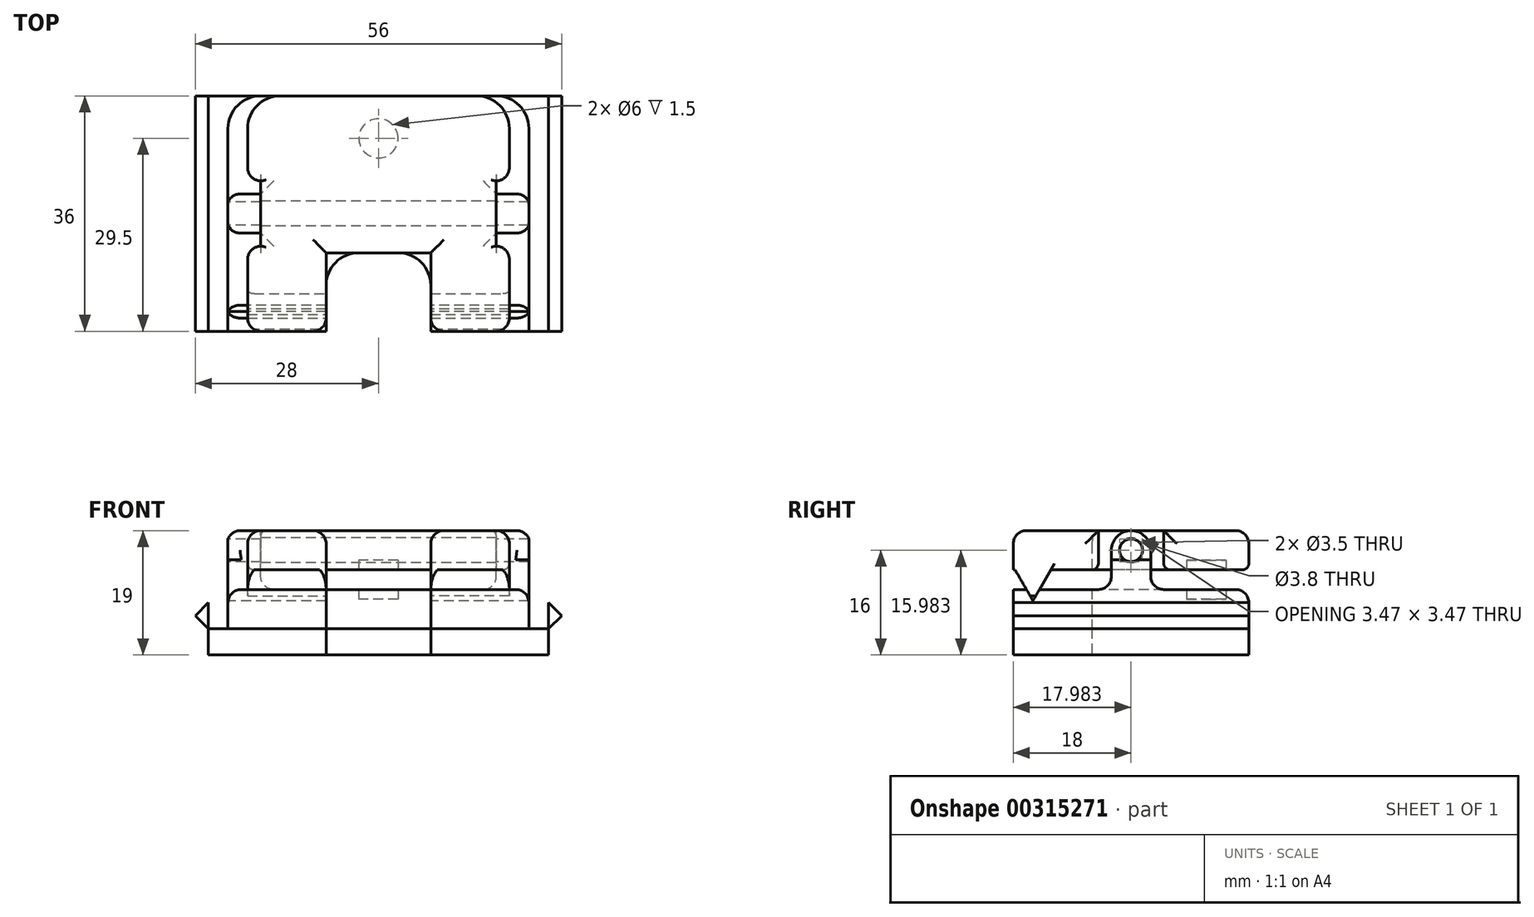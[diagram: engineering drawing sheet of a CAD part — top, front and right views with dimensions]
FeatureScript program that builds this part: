
annotation { "Feature Type Name" : "Feature", "Feature Type Description" : "" }
export const myFeature = defineFeature(function(context is Context, id is Id, definition is map)
    precondition{}
    {
        {
            var Q0;
            Q0=qCreatedBy(makeId("Top.planeOp"),FACE);
            var sketch = newSketch(context, id + "F0", { "sketchPlane" : qUnion([Q0])});
            skLineSegment(sketch, "E0.bottom", {"start": v(23, -18) * mm, "end": v(8, -18) * mm});
            skLineSegment(sketch, "E0.top", {"start": v(23, 18) * mm, "end": v(-23, 18) * mm});
            skLineSegment(sketch, "E0.left", {"start": v(23, -18) * mm, "end": v(23, 18) * mm});
            skLineSegment(sketch, "E0.right", {"start": v(-23, -18) * mm, "end": v(-23, 18) * mm});
            skPoint(sketch, "E0.middle", {"position": v(0, 0) * mm});
            skPoint(sketch, "E1.endSnap0", {"position": v(0, -18) * mm});
            skLineSegment(sketch, "E2", {"start": v(0, -6) * mm, "end": v(8, -6) * mm});
            skLineSegment(sketch, "E3", {"start": v(0, -6) * mm, "end": v(-8, -6) * mm});
            skLineSegment(sketch, "E4", {"start": v(-8, -6) * mm, "end": v(-8, -18) * mm});
            skLineSegment(sketch, "E5", {"start": v(8, -6) * mm, "end": v(8, -18) * mm});
            skLineSegment(sketch, "E6.trimOffspring", {"start": v(-8, -18) * mm, "end": v(-23, -18) * mm});
            skSolve(sketch);
        }
        {
            var Q0;
            Q0 = qSketchRegion(id + "F0", true);
            extrude(context, id + "F1", {"entities" : qUnion([Q0]), "depth" : 6 * mm});
        }
        {
            var Q0;
            Q0=qCreatedBy(makeId("Right.planeOp"),FACE);
            var sketch = newSketch(context, id + "F2", { "sketchPlane" : qUnion([Q0])});
            skCircle(sketch, "E7.cCircle", {"center": v(0, 0) * mm, "radius": 3.36 * mm, "construction": true});
            skLineSegment(sketch, "E7.0", {"start": v(5.82, -3.36) * mm, "end": v(-5.82, -3.36) * mm});
            skLineSegment(sketch, "E7.1", {"start": v(-5.82, -3.36) * mm, "end": v(0, 6.72) * mm});
            skLineSegment(sketch, "E7.2", {"start": v(0, 6.72) * mm, "end": v(5.82, -3.36) * mm});
            skPoint(sketch, "E7.0.midPoint", {"position": v(0, -3.36) * mm});
            skSolve(sketch);
        }
        {
            var Q0;
            Q0 = qSketchRegion(id + "F2", true);
            extrude(context, id + "F3", {"entities" : qUnion([Q0]), "endBound" : BoundingType.SYMMETRIC, "depth" : 80 * mm});
        }
        {
            var Q0;
            Q0=qCreatedBy(makeId("Top.planeOp"),FACE);
            var sketch = newSketch(context, id + "F4", { "sketchPlane" : qUnion([Q0])});
            skLineSegment(sketch, "E8", {"start": v(0, 0) * mm, "end": v(58.84, 0) * mm, "construction": true});
            skSolve(sketch);
        }
        {
            var Q0;
            Q0=makeQuery(id+"F3.opExtrude","SWEPT_BODY",BODY,{"disambiguationData":[OSD([sQuery(id+"F2.wireOp",EDGE,"E7.0"),sQuery(id+"F2.wireOp",EDGE,"E7.1"),sQuery(id+"F2.wireOp",EDGE,"E7.2")])]});
            transform(context, id + "F5", {"entities" : qUnion([Q0]), "transformType" : TransformType.COPY});
        }
        {
            var Q0;
            Q0=makeQuery(id+"F3.opExtrude","SWEPT_BODY",BODY,{"disambiguationData":[OSD([sQuery(id+"F2.wireOp",EDGE,"E7.0"),sQuery(id+"F2.wireOp",EDGE,"E7.1"),sQuery(id+"F2.wireOp",EDGE,"E7.2")])]});
            var Q1;
            Q1=sQuery(id+"F4.wireOp",EDGE,"E8");
            transform(context, id + "F6", {"entities" : qUnion([Q0]), "transformType" : TransformType.ROTATION, "transformAxis" : qUnion([Q1]), "angle" : 180 * degree, "makeCopy" : false});
        }
        {
            var Q0;
            Q0=makeQuery(id+"F3.opExtrude","SWEPT_BODY",BODY,{"disambiguationData":[OSD([sQuery(id+"F2.wireOp",EDGE,"E7.0"),sQuery(id+"F2.wireOp",EDGE,"E7.1"),sQuery(id+"F2.wireOp",EDGE,"E7.2")])]});
            transform(context, id + "F7", {"entities" : qUnion([Q0]), "transformType" : TransformType.TRANSLATION_3D, "dx" : 0 * mm, "dy" : -15 * mm, "dz" : 11 * mm, "makeCopy" : false});
        }
        {
            var Q0;
            Q0=qCreatedBy(makeId("Top.planeOp"),FACE);
            var sketch = newSketch(context, id + "F8", { "sketchPlane" : qUnion([Q0])});
            skLineSegment(sketch, "E9.bottom", {"start": v(45, -5) * mm, "end": v(-45, -5) * mm});
            skLineSegment(sketch, "E9.top", {"start": v(45, 5) * mm, "end": v(-45, 5) * mm});
            skLineSegment(sketch, "E9.left", {"start": v(45, -5) * mm, "end": v(45, 5) * mm});
            skLineSegment(sketch, "E9.right", {"start": v(-45, -5) * mm, "end": v(-45, 5) * mm});
            skPoint(sketch, "E9.middle", {"position": v(0, 0) * mm});
            skSolve(sketch);
        }
        {
            var Q0;
            Q0 = qSketchRegion(id + "F8", true);
            extrude(context, id + "F9", {"entities" : qUnion([Q0]), "depth" : 10 * mm});
        }
        {
            var Q0;
            Q0=makeQuery(id+"F9.opExtrude","SWEPT_BODY",BODY,{"disambiguationData":[OSD([sQuery(id+"F8.wireOp",EDGE,"E9.bottom"),sQuery(id+"F8.wireOp",EDGE,"E9.top"),sQuery(id+"F8.wireOp",EDGE,"E9.left"),sQuery(id+"F8.wireOp",EDGE,"E9.right")])]});
            transform(context, id + "F10", {"entities" : qUnion([Q0]), "transformType" : TransformType.TRANSLATION_3D, "dx" : 0 * mm, "dy" : 0 * mm, "dz" : 6 * mm, "makeCopy" : false});
        }
        {
            var Q0;
            Q0=makeQuery(id+"F9.opExtrude","SWEPT_BODY",BODY,{"disambiguationData":[OSD([sQuery(id+"F8.wireOp",EDGE,"E9.bottom"),sQuery(id+"F8.wireOp",EDGE,"E9.top"),sQuery(id+"F8.wireOp",EDGE,"E9.left"),sQuery(id+"F8.wireOp",EDGE,"E9.right")])]});
            var Q1;
            Q1=makeQuery(id+"F5.opPattern","COPY",BODY,{"derivedFrom":makeQuery(id+"F3.opExtrude","SWEPT_BODY",BODY,{"disambiguationData":[OSD([sQuery(id+"F2.wireOp",EDGE,"E7.0"),sQuery(id+"F2.wireOp",EDGE,"E7.1"),sQuery(id+"F2.wireOp",EDGE,"E7.2")])]}),"instanceName":"1"});
            booleanBodies(context, id + "F11", {"operationType" : BooleanOperationType.SUBTRACTION, "tools" : qUnion([Q0]), "targets" : qUnion([Q1])});
        }
        {
            var Q0;
            Q0=makeQuery(id+"F3.opExtrude","SWEPT_BODY",BODY,{"disambiguationData":[OSD([sQuery(id+"F2.wireOp",EDGE,"E7.0"),sQuery(id+"F2.wireOp",EDGE,"E7.1"),sQuery(id+"F2.wireOp",EDGE,"E7.2")])]});
            var Q1;
            Q1=makeQuery(id+"F1.opExtrude","SWEPT_BODY",BODY,{"disambiguationData":[OSD([sQuery(id+"F0.wireOp",EDGE,"E0.bottom"),sQuery(id+"F0.wireOp",EDGE,"E0.top"),sQuery(id+"F0.wireOp",EDGE,"E0.left"),sQuery(id+"F0.wireOp",EDGE,"E0.right"),sQuery(id+"F0.wireOp",EDGE,"E2"),sQuery(id+"F0.wireOp",EDGE,"E3"),sQuery(id+"F0.wireOp",EDGE,"E4"),sQuery(id+"F0.wireOp",EDGE,"E5"),sQuery(id+"F0.wireOp",EDGE,"E6.trimOffspring")])]});
            booleanBodies(context, id + "F12", {"operationType" : BooleanOperationType.SUBTRACTION, "tools" : qUnion([Q0]), "targets" : qUnion([Q1])});
        }
        {
            var Q0;
            Q0=qCreatedBy(makeId("Top.planeOp"),FACE);
            var sketch = newSketch(context, id + "F13", { "sketchPlane" : qUnion([Q0])});
            skLineSegment(sketch, "E10", {"start": v(0, 0) * mm, "end": v(55.34, 0) * mm, "construction": true});
            skSolve(sketch);
        }
        {
            var Q0;
            Q0=makeQuery(id+"F5.opPattern","COPY",BODY,{"derivedFrom":makeQuery(id+"F3.opExtrude","SWEPT_BODY",BODY,{"disambiguationData":[OSD([sQuery(id+"F2.wireOp",EDGE,"E7.0"),sQuery(id+"F2.wireOp",EDGE,"E7.1"),sQuery(id+"F2.wireOp",EDGE,"E7.2")])]}),"instanceName":"1"});
            var Q1;
            Q1=sQuery(id+"F13.wireOp",EDGE,"E10");
            transform(context, id + "F14", {"entities" : qUnion([Q0]), "transformType" : TransformType.ROTATION, "transformAxis" : qUnion([Q1]), "angle" : 180 * degree, "makeCopy" : false});
        }
        {
            var Q0;
            Q0=makeQuery(id+"F5.opPattern","COPY",BODY,{"derivedFrom":makeQuery(id+"F3.opExtrude","SWEPT_BODY",BODY,{"disambiguationData":[OSD([sQuery(id+"F2.wireOp",EDGE,"E7.0"),sQuery(id+"F2.wireOp",EDGE,"E7.1"),sQuery(id+"F2.wireOp",EDGE,"E7.2")])]}),"instanceName":"1"});
            transform(context, id + "F15", {"entities" : qUnion([Q0]), "transformType" : TransformType.TRANSLATION_3D, "dx" : 0 * mm, "dy" : -15 * mm, "dz" : 11 * mm, "makeCopy" : false});
        }
        {
            var Q0;
            Q0=qCreatedBy(makeId("Top.planeOp"),FACE);
            var sketch = newSketch(context, id + "F16", { "sketchPlane" : qUnion([Q0])});
            skLineSegment(sketch, "E11.bottom", {"start": v(20, -18) * mm, "end": v(-20, -18) * mm});
            skLineSegment(sketch, "E11.top", {"start": v(20, 18) * mm, "end": v(-20, 18) * mm});
            skLineSegment(sketch, "E11.left", {"start": v(20, -18) * mm, "end": v(20, 18) * mm});
            skLineSegment(sketch, "E11.right", {"start": v(-20, -18) * mm, "end": v(-20, 18) * mm});
            skPoint(sketch, "E11.middle", {"position": v(0, 0) * mm});
            skSolve(sketch);
        }
        {
            var Q0;
            Q0 = qSketchRegion(id + "F16", true);
            extrude(context, id + "F17", {"entities" : qUnion([Q0]), "depth" : 6 * mm});
        }
        {
            var Q0;
            Q0=qCreatedBy(makeId("Top.planeOp"),FACE);
            var sketch = newSketch(context, id + "F18", { "sketchPlane" : qUnion([Q0])});
            skLineSegment(sketch, "E12", {"start": v(0, 0) * mm, "end": v(0, -6) * mm});
            skLineSegment(sketch, "E13", {"start": v(0, -6) * mm, "end": v(8, -6) * mm});
            skLineSegment(sketch, "E14", {"start": v(8, -6) * mm, "end": v(8, -18) * mm});
            skLineSegment(sketch, "E15", {"start": v(8, -18) * mm, "end": v(-8, -18) * mm});
            skLineSegment(sketch, "E16", {"start": v(-8, -18) * mm, "end": v(-8, -6) * mm});
            skLineSegment(sketch, "E17", {"start": v(-8, -6) * mm, "end": v(0, -6) * mm});
            skSolve(sketch);
        }
        {
            var Q0;
            Q0 = qSketchRegion(id + "F18", true);
            extrude(context, id + "F19", {"entities" : qUnion([Q0]), "depth" : 25 * mm});
        }
        {
            var Q0;
            Q0=makeQuery(id+"F19.opExtrude","SWEPT_BODY",BODY,{"disambiguationData":[OSD([sQuery(id+"F18.wireOp",EDGE,"E13"),sQuery(id+"F18.wireOp",EDGE,"E14"),sQuery(id+"F18.wireOp",EDGE,"E15"),sQuery(id+"F18.wireOp",EDGE,"E16"),sQuery(id+"F18.wireOp",EDGE,"E17")])]});
            var Q1;
            Q1=makeQuery(id+"F17.opExtrude","SWEPT_BODY",BODY,{"disambiguationData":[OSD([sQuery(id+"F16.wireOp",EDGE,"E11.bottom"),sQuery(id+"F16.wireOp",EDGE,"E11.top"),sQuery(id+"F16.wireOp",EDGE,"E11.left"),sQuery(id+"F16.wireOp",EDGE,"E11.right")])]});
            booleanBodies(context, id + "F20", {"operationType" : BooleanOperationType.SUBTRACTION, "tools" : qUnion([Q0]), "targets" : qUnion([Q1])});
        }
        {
            var Q0;
            Q0=makeQuery(id+"F17.opExtrude","SWEPT_BODY",BODY,{"disambiguationData":[OSD([sQuery(id+"F16.wireOp",EDGE,"E11.bottom"),sQuery(id+"F16.wireOp",EDGE,"E11.top"),sQuery(id+"F16.wireOp",EDGE,"E11.left"),sQuery(id+"F16.wireOp",EDGE,"E11.right")])]});
            transform(context, id + "F21", {"entities" : qUnion([Q0]), "transformType" : TransformType.TRANSLATION_3D, "dx" : 0 * mm, "dy" : 0 * mm, "dz" : 9 * mm, "makeCopy" : false});
        }
        {
            var Q0;
            Q0=qCreatedBy(makeId("Top.planeOp"),FACE);
            var sketch = newSketch(context, id + "F22", { "sketchPlane" : qUnion([Q0])});
            skLineSegment(sketch, "E18", {"start": v(0, 0) * mm, "end": v(0, -9) * mm});
            skLineSegment(sketch, "E19", {"start": v(0, -9) * mm, "end": v(8, -9) * mm});
            skLineSegment(sketch, "E20", {"start": v(8, -9) * mm, "end": v(8, -21) * mm});
            skLineSegment(sketch, "E21", {"start": v(8, -21) * mm, "end": v(-8, -21) * mm});
            skLineSegment(sketch, "E22", {"start": v(-8, -21) * mm, "end": v(-8, -9) * mm});
            skLineSegment(sketch, "E23", {"start": v(-8, -9) * mm, "end": v(0, -9) * mm});
            skLineSegment(sketch, "E24", {"start": v(8, -9) * mm, "end": v(20, -9) * mm});
            skLineSegment(sketch, "E25", {"start": v(20, -9) * mm, "end": v(20, -21) * mm});
            skLineSegment(sketch, "E26", {"start": v(20, -21) * mm, "end": v(42, -21) * mm});
            skLineSegment(sketch, "E27", {"start": v(42, -21) * mm, "end": v(42, -9) * mm});
            skLineSegment(sketch, "E28", {"start": v(42, -9) * mm, "end": v(20, -9) * mm});
            skLineSegment(sketch, "E29", {"start": v(-8, -9) * mm, "end": v(-20, -9) * mm});
            skLineSegment(sketch, "E30", {"start": v(-20, -9) * mm, "end": v(-20, -21) * mm});
            skLineSegment(sketch, "E31", {"start": v(-20, -21) * mm, "end": v(-42, -21) * mm});
            skLineSegment(sketch, "E32", {"start": v(-42, -21) * mm, "end": v(-42, -9) * mm});
            skLineSegment(sketch, "E33", {"start": v(-42, -9) * mm, "end": v(-20, -9) * mm});
            skSolve(sketch);
        }
        {
            var Q0;
            Q0 = qSketchRegion(id + "F22", true);
            extrude(context, id + "F23", {"entities" : qUnion([Q0]), "depth" : 25 * mm});
        }
        {
            var Q0;
            Q0=makeQuery(id+"F23.opExtrude","SWEPT_BODY",BODY,{"disambiguationData":[OSD([sQuery(id+"F22.wireOp",EDGE,"E30"),sQuery(id+"F22.wireOp",EDGE,"E31"),sQuery(id+"F22.wireOp",EDGE,"E32"),sQuery(id+"F22.wireOp",EDGE,"E33")])]});
            var Q1;
            Q1=makeQuery(id+"F23.opExtrude","SWEPT_BODY",BODY,{"disambiguationData":[OSD([sQuery(id+"F22.wireOp",EDGE,"E19"),sQuery(id+"F22.wireOp",EDGE,"E20"),sQuery(id+"F22.wireOp",EDGE,"E21"),sQuery(id+"F22.wireOp",EDGE,"E22"),sQuery(id+"F22.wireOp",EDGE,"E23")])]});
            var Q2;
            Q2=makeQuery(id+"F23.opExtrude","SWEPT_BODY",BODY,{"disambiguationData":[OSD([sQuery(id+"F22.wireOp",EDGE,"E25"),sQuery(id+"F22.wireOp",EDGE,"E26"),sQuery(id+"F22.wireOp",EDGE,"E27"),sQuery(id+"F22.wireOp",EDGE,"E28")])]});
            var Q3;
            Q3=makeQuery(id+"F5.opPattern","COPY",BODY,{"derivedFrom":makeQuery(id+"F3.opExtrude","SWEPT_BODY",BODY,{"disambiguationData":[OSD([sQuery(id+"F2.wireOp",EDGE,"E7.0"),sQuery(id+"F2.wireOp",EDGE,"E7.1"),sQuery(id+"F2.wireOp",EDGE,"E7.2")])]}),"instanceName":"1"});
            booleanBodies(context, id + "F24", {"operationType" : BooleanOperationType.SUBTRACTION, "tools" : qUnion([Q0, Q1, Q2]), "targets" : qUnion([Q3])});
        }
        {
            var Q0;
            Q0=qCreatedBy(makeId("Top.planeOp"),FACE);
            var sketch = newSketch(context, id + "F25", { "sketchPlane" : qUnion([Q0])});
            skLineSegment(sketch, "E34", {"start": v(0, 0) * mm, "end": v(20, 0) * mm});
            skLineSegment(sketch, "E35", {"start": v(20, 0) * mm, "end": v(20, -18) * mm});
            skLineSegment(sketch, "E36", {"start": v(20, -18) * mm, "end": v(20, -23) * mm});
            skLineSegment(sketch, "E37", {"start": v(20, -23) * mm, "end": v(-20, -23) * mm});
            skLineSegment(sketch, "E38", {"start": v(-20, -23) * mm, "end": v(-20, -18) * mm});
            skLineSegment(sketch, "E39", {"start": v(-20, -18) * mm, "end": v(20, -18) * mm});
            skSolve(sketch);
        }
        {
            var Q0;
            Q0 = qSketchRegion(id + "F25", true);
            extrude(context, id + "F26", {"entities" : qUnion([Q0]), "depth" : 25 * mm});
        }
        {
            var Q0;
            Q0=makeQuery(id+"F26.opExtrude","SWEPT_BODY",BODY,{"disambiguationData":[OSD([sQuery(id+"F25.wireOp",EDGE,"E36"),sQuery(id+"F25.wireOp",EDGE,"E37"),sQuery(id+"F25.wireOp",EDGE,"E38"),sQuery(id+"F25.wireOp",EDGE,"E39")])]});
            var Q1;
            Q1=makeQuery(id+"F24.opBoolean","SPLIT",BODY,{"disambiguationData":[OD(1.0)],"derivedFrom":makeQuery(id+"F5.opPattern","COPY",BODY,{"derivedFrom":makeQuery(id+"F3.opExtrude","SWEPT_BODY",BODY,{"disambiguationData":[OSD([sQuery(id+"F2.wireOp",EDGE,"E7.0"),sQuery(id+"F2.wireOp",EDGE,"E7.1"),sQuery(id+"F2.wireOp",EDGE,"E7.2")])]}),"instanceName":"1"})});
            var Q2;
            Q2=makeQuery(id+"F24.opBoolean","SPLIT",BODY,{"disambiguationData":[OD(0.0)],"derivedFrom":makeQuery(id+"F5.opPattern","COPY",BODY,{"derivedFrom":makeQuery(id+"F3.opExtrude","SWEPT_BODY",BODY,{"disambiguationData":[OSD([sQuery(id+"F2.wireOp",EDGE,"E7.0"),sQuery(id+"F2.wireOp",EDGE,"E7.1"),sQuery(id+"F2.wireOp",EDGE,"E7.2")])]}),"instanceName":"1"})});
            booleanBodies(context, id + "F27", {"operationType" : BooleanOperationType.SUBTRACTION, "tools" : qUnion([Q0]), "targets" : qUnion([Q1, Q2])});
        }
        {
            var Q0;
            Q0=makeQuery(id+"F24.opBoolean","SPLIT",BODY,{"disambiguationData":[OD(0.0)],"derivedFrom":makeQuery(id+"F5.opPattern","COPY",BODY,{"derivedFrom":makeQuery(id+"F3.opExtrude","SWEPT_BODY",BODY,{"disambiguationData":[OSD([sQuery(id+"F2.wireOp",EDGE,"E7.0"),sQuery(id+"F2.wireOp",EDGE,"E7.1"),sQuery(id+"F2.wireOp",EDGE,"E7.2")])]}),"instanceName":"1"})});
            var Q1;
            Q1=makeQuery(id+"F24.opBoolean","SPLIT",BODY,{"disambiguationData":[OD(1.0)],"derivedFrom":makeQuery(id+"F5.opPattern","COPY",BODY,{"derivedFrom":makeQuery(id+"F3.opExtrude","SWEPT_BODY",BODY,{"disambiguationData":[OSD([sQuery(id+"F2.wireOp",EDGE,"E7.0"),sQuery(id+"F2.wireOp",EDGE,"E7.1"),sQuery(id+"F2.wireOp",EDGE,"E7.2")])]}),"instanceName":"1"})});
            var Q2;
            Q2=makeQuery(id+"F17.opExtrude","SWEPT_BODY",BODY,{"disambiguationData":[OSD([sQuery(id+"F16.wireOp",EDGE,"E11.bottom"),sQuery(id+"F16.wireOp",EDGE,"E11.top"),sQuery(id+"F16.wireOp",EDGE,"E11.left"),sQuery(id+"F16.wireOp",EDGE,"E11.right")])]});
            booleanBodies(context, id + "F28", {"operationType" : BooleanOperationType.UNION, "tools" : qUnion([Q0, Q1, Q2])});
        }
        {
            var Q0;
            Q0=qCreatedBy(makeId("Right.planeOp"),FACE);
            var sketch = newSketch(context, id + "F29", { "sketchPlane" : qUnion([Q0])});
            skArc(sketch, "E40", {"start": v(3, 12) * mm, "mid": v(0, 15) * mm, "end": v(-3, 12) * mm});
            skLineSegment(sketch, "E41", {"start": v(0, 0) * mm, "end": v(3, 0) * mm});
            skLineSegment(sketch, "E42", {"start": v(3, 0) * mm, "end": v(3, 12) * mm});
            skLineSegment(sketch, "E43", {"start": v(0, 0) * mm, "end": v(-3, 0) * mm});
            skLineSegment(sketch, "E44", {"start": v(-3, 0) * mm, "end": v(-3, 12) * mm});
            skCircle(sketch, "E45", {"center": v(0, 12) * mm, "radius": 1.75 * mm});
            skSolve(sketch);
        }
        {
            var Q0;
            Q0 = qSketchRegion(id + "F29", true);
            extrude(context, id + "F30", {"entities" : qUnion([Q0]), "endBound" : BoundingType.SYMMETRIC, "depth" : 5 * mm});
        }
        {
            var Q0;
            Q0=makeQuery(id+"F30.opExtrude","SWEPT_BODY",BODY,{"disambiguationData":[OSD([sQuery(id+"F29.wireOp",EDGE,"E40"),sQuery(id+"F29.wireOp",EDGE,"E41"),sQuery(id+"F29.wireOp",EDGE,"E42"),sQuery(id+"F29.wireOp",EDGE,"E43"),sQuery(id+"F29.wireOp",EDGE,"E44"),sQuery(id+"F29.wireOp",EDGE,"E45")])]});
            transform(context, id + "F31", {"entities" : qUnion([Q0]), "transformType" : TransformType.COPY});
        }
        {
            var Q0;
            Q0=makeQuery(id+"F31.opPattern","COPY",BODY,{"derivedFrom":makeQuery(id+"F30.opExtrude","SWEPT_BODY",BODY,{"disambiguationData":[OSD([sQuery(id+"F29.wireOp",EDGE,"E40"),sQuery(id+"F29.wireOp",EDGE,"E41"),sQuery(id+"F29.wireOp",EDGE,"E42"),sQuery(id+"F29.wireOp",EDGE,"E43"),sQuery(id+"F29.wireOp",EDGE,"E44"),sQuery(id+"F29.wireOp",EDGE,"E45")])]}),"instanceName":"1"});
            transform(context, id + "F32", {"entities" : qUnion([Q0]), "transformType" : TransformType.TRANSLATION_3D, "dx" : 20.5 * mm, "dy" : 0 * mm, "dz" : 0 * mm, "makeCopy" : false});
        }
        {
            var Q0;
            Q0=makeQuery(id+"F30.opExtrude","SWEPT_BODY",BODY,{"disambiguationData":[OSD([sQuery(id+"F29.wireOp",EDGE,"E40"),sQuery(id+"F29.wireOp",EDGE,"E41"),sQuery(id+"F29.wireOp",EDGE,"E42"),sQuery(id+"F29.wireOp",EDGE,"E43"),sQuery(id+"F29.wireOp",EDGE,"E44"),sQuery(id+"F29.wireOp",EDGE,"E45")])]});
            transform(context, id + "F33", {"entities" : qUnion([Q0]), "transformType" : TransformType.TRANSLATION_3D, "dx" : -20.5 * mm, "dy" : 0 * mm, "dz" : 0 * mm, "makeCopy" : false});
        }
        {
            var Q0;
            Q0=qCreatedBy(makeId("Top.planeOp"),FACE);
            var sketch = newSketch(context, id + "F34", { "sketchPlane" : qUnion([Q0])});
            skLineSegment(sketch, "E46.bottom", {"start": v(3, -5) * mm, "end": v(-3, -5) * mm});
            skLineSegment(sketch, "E46.top", {"start": v(3, 5) * mm, "end": v(-3, 5) * mm});
            skLineSegment(sketch, "E46.left", {"start": v(3, -5) * mm, "end": v(3, 5) * mm});
            skLineSegment(sketch, "E46.right", {"start": v(-3, -5) * mm, "end": v(-3, 5) * mm});
            skPoint(sketch, "E46.middle", {"position": v(0, 0) * mm});
            skSolve(sketch);
        }
        {
            var Q0;
            Q0 = qSketchRegion(id + "F34", true);
            extrude(context, id + "F35", {"entities" : qUnion([Q0]), "depth" : 25 * mm});
        }
        {
            var Q0;
            Q0=makeQuery(id+"F35.opExtrude","SWEPT_BODY",BODY,{"disambiguationData":[OSD([sQuery(id+"F34.wireOp",EDGE,"E46.bottom"),sQuery(id+"F34.wireOp",EDGE,"E46.top"),sQuery(id+"F34.wireOp",EDGE,"E46.left"),sQuery(id+"F34.wireOp",EDGE,"E46.right")])]});
            transform(context, id + "F36", {"entities" : qUnion([Q0]), "transformType" : TransformType.COPY});
        }
        {
            var Q0;
            Q0=makeQuery(id+"F36.opPattern","COPY",BODY,{"derivedFrom":makeQuery(id+"F35.opExtrude","SWEPT_BODY",BODY,{"disambiguationData":[OSD([sQuery(id+"F34.wireOp",EDGE,"E46.bottom"),sQuery(id+"F34.wireOp",EDGE,"E46.top"),sQuery(id+"F34.wireOp",EDGE,"E46.left"),sQuery(id+"F34.wireOp",EDGE,"E46.right")])]}),"instanceName":"1"});
            transform(context, id + "F37", {"entities" : qUnion([Q0]), "transformType" : TransformType.TRANSLATION_3D, "dx" : 21 * mm, "dy" : 0 * mm, "dz" : 0 * mm, "makeCopy" : false});
        }
        {
            var Q0;
            Q0=makeQuery(id+"F35.opExtrude","SWEPT_BODY",BODY,{"disambiguationData":[OSD([sQuery(id+"F34.wireOp",EDGE,"E46.bottom"),sQuery(id+"F34.wireOp",EDGE,"E46.top"),sQuery(id+"F34.wireOp",EDGE,"E46.left"),sQuery(id+"F34.wireOp",EDGE,"E46.right")])]});
            transform(context, id + "F38", {"entities" : qUnion([Q0]), "transformType" : TransformType.TRANSLATION_3D, "dx" : -21 * mm, "dy" : 0 * mm, "dz" : 0 * mm, "makeCopy" : false});
        }
        {
            var Q0;
            Q0=makeQuery(id+"F35.opExtrude","SWEPT_BODY",BODY,{"disambiguationData":[OSD([sQuery(id+"F34.wireOp",EDGE,"E46.bottom"),sQuery(id+"F34.wireOp",EDGE,"E46.top"),sQuery(id+"F34.wireOp",EDGE,"E46.left"),sQuery(id+"F34.wireOp",EDGE,"E46.right")])]});
            var Q1;
            Q1=makeQuery(id+"F36.opPattern","COPY",BODY,{"derivedFrom":makeQuery(id+"F35.opExtrude","SWEPT_BODY",BODY,{"disambiguationData":[OSD([sQuery(id+"F34.wireOp",EDGE,"E46.bottom"),sQuery(id+"F34.wireOp",EDGE,"E46.top"),sQuery(id+"F34.wireOp",EDGE,"E46.left"),sQuery(id+"F34.wireOp",EDGE,"E46.right")])]}),"instanceName":"1"});
            var Q2;
            Q2=makeQuery(id+"F24.opBoolean","SPLIT",BODY,{"disambiguationData":[OD(0.0)],"derivedFrom":makeQuery(id+"F5.opPattern","COPY",BODY,{"derivedFrom":makeQuery(id+"F3.opExtrude","SWEPT_BODY",BODY,{"disambiguationData":[OSD([sQuery(id+"F2.wireOp",EDGE,"E7.0"),sQuery(id+"F2.wireOp",EDGE,"E7.1"),sQuery(id+"F2.wireOp",EDGE,"E7.2")])]}),"instanceName":"1"})});
            booleanBodies(context, id + "F39", {"operationType" : BooleanOperationType.SUBTRACTION, "tools" : qUnion([Q0, Q1]), "targets" : qUnion([Q2])});
        }
        {
            var Q0;
            Q0=qCreatedBy(makeId("Right.planeOp"),FACE);
            var sketch = newSketch(context, id + "F40", { "sketchPlane" : qUnion([Q0])});
            skLineSegment(sketch, "E47", {"start": v(0, 0) * mm, "end": v(0, 12) * mm});
            skCircle(sketch, "E48", {"center": v(0, 12) * mm, "radius": 1.9 * mm});
            skSolve(sketch);
        }
        {
            var Q0;
            Q0 = qSketchRegion(id + "F40", true);
            extrude(context, id + "F41", {"entities" : qUnion([Q0]), "endBound" : BoundingType.SYMMETRIC, "depth" : 80 * mm});
        }
        {
            var Q0;
            Q0=makeQuery(id+"F41.opExtrude","SWEPT_BODY",BODY,{"disambiguationData":[OSD([sQuery(id+"F40.wireOp",EDGE,"E48")])]});
            var Q1;
            Q1=makeQuery(id+"F24.opBoolean","SPLIT",BODY,{"disambiguationData":[OD(0.0)],"derivedFrom":makeQuery(id+"F5.opPattern","COPY",BODY,{"derivedFrom":makeQuery(id+"F3.opExtrude","SWEPT_BODY",BODY,{"disambiguationData":[OSD([sQuery(id+"F2.wireOp",EDGE,"E7.0"),sQuery(id+"F2.wireOp",EDGE,"E7.1"),sQuery(id+"F2.wireOp",EDGE,"E7.2")])]}),"instanceName":"1"})});
            booleanBodies(context, id + "F42", {"operationType" : BooleanOperationType.SUBTRACTION, "tools" : qUnion([Q0]), "targets" : qUnion([Q1])});
        }
        {
            var Q0;
            Q0=qCreatedBy(makeId("Top.planeOp"),FACE);
            var sketch = newSketch(context, id + "F43", { "sketchPlane" : qUnion([Q0])});
            skCircle(sketch, "E49", {"center": v(0, 12.5) * mm, "radius": 3 * mm});
            skSolve(sketch);
        }
        {
            var Q0;
            Q0 = qSketchRegion(id + "F43", true);
            extrude(context, id + "F44", {"entities" : qUnion([Q0]), "depth" : 6 * mm});
        }
        {
            var Q0;
            Q0=makeQuery(id+"F44.opExtrude","SWEPT_BODY",BODY,{"disambiguationData":[OSD([sQuery(id+"F43.wireOp",EDGE,"E49")])]});
            transform(context, id + "F45", {"entities" : qUnion([Q0]), "transformType" : TransformType.TRANSLATION_3D, "dx" : 0 * mm, "dy" : -1 * mm, "dz" : 4.5 * mm, "makeCopy" : false});
        }
        {
            var Q0;
            Q0=makeQuery(id+"F44.opExtrude","SWEPT_BODY",BODY,{"disambiguationData":[OSD([sQuery(id+"F43.wireOp",EDGE,"E49")])]});
            var Q1;
            Q1=makeQuery(id+"F1.opExtrude","SWEPT_BODY",BODY,{"disambiguationData":[OSD([sQuery(id+"F0.wireOp",EDGE,"E0.bottom"),sQuery(id+"F0.wireOp",EDGE,"E0.top"),sQuery(id+"F0.wireOp",EDGE,"E0.left"),sQuery(id+"F0.wireOp",EDGE,"E0.right"),sQuery(id+"F0.wireOp",EDGE,"E2"),sQuery(id+"F0.wireOp",EDGE,"E3"),sQuery(id+"F0.wireOp",EDGE,"E4"),sQuery(id+"F0.wireOp",EDGE,"E5"),sQuery(id+"F0.wireOp",EDGE,"E6.trimOffspring")])]});
            var Q2;
            Q2=makeQuery(id+"F24.opBoolean","SPLIT",BODY,{"disambiguationData":[OD(0.0)],"derivedFrom":makeQuery(id+"F5.opPattern","COPY",BODY,{"derivedFrom":makeQuery(id+"F3.opExtrude","SWEPT_BODY",BODY,{"disambiguationData":[OSD([sQuery(id+"F2.wireOp",EDGE,"E7.0"),sQuery(id+"F2.wireOp",EDGE,"E7.1"),sQuery(id+"F2.wireOp",EDGE,"E7.2")])]}),"instanceName":"1"})});
            booleanBodies(context, id + "F46", {"operationType" : BooleanOperationType.SUBTRACTION, "tools" : qUnion([Q0]), "targets" : qUnion([Q1, Q2])});
        }
        {
            var Q0;
            Q0=qCreatedBy(makeId("Front.planeOp"),FACE);
            var sketch = newSketch(context, id + "F47", { "sketchPlane" : qUnion([Q0])});
            skLineSegment(sketch, "E50", {"start": v(0, 0) * mm, "end": v(10, 0) * mm});
            skLineSegment(sketch, "E51", {"start": v(10, 0) * mm, "end": v(10, 1.5) * mm});
            skText(sketch, "E52", { "text": "SF", "fontName": "OpenSans-Bold.ttf"});
            const initialGuessF47  = {"E52": [0.01, 0.0015, 1, 0, 0.0035]};
            skSetInitialGuess(sketch, initialGuessF47);
            skSolve(sketch);
        }
        {
            var Q0;
            Q0 = qSketchRegion(id + "F47", true);
            extrude(context, id + "F48", {"entities" : qUnion([Q0]), "depth" : 3 * mm});
        }
        {
            var Q0;
            Q0=makeQuery(id+"F48.opExtrude","SWEPT_BODY",BODY,{"disambiguationData":[OSD([sQuery(id+"F47.wireOp",EDGE,"E52.sketch_text.stroke-28"),sQuery(id+"F47.wireOp",EDGE,"E52.sketch_text.stroke-29"),sQuery(id+"F47.wireOp",EDGE,"E52.sketch_text.stroke-30"),sQuery(id+"F47.wireOp",EDGE,"E52.sketch_text.stroke-31"),sQuery(id+"F47.wireOp",EDGE,"E52.sketch_text.stroke-32"),sQuery(id+"F47.wireOp",EDGE,"E52.sketch_text.stroke-33"),sQuery(id+"F47.wireOp",EDGE,"E52.sketch_text.stroke-34"),sQuery(id+"F47.wireOp",EDGE,"E52.sketch_text.stroke-35"),sQuery(id+"F47.wireOp",EDGE,"E52.sketch_text.stroke-36"),sQuery(id+"F47.wireOp",EDGE,"E52.sketch_text.stroke-37")])]});
            var Q1;
            Q1=makeQuery(id+"F48.opExtrude","SWEPT_BODY",BODY,{"disambiguationData":[OSD([sQuery(id+"F47.wireOp",EDGE,"E52.sketch_text.stroke-0"),sQuery(id+"F47.wireOp",EDGE,"E52.sketch_text.stroke-1"),sQuery(id+"F47.wireOp",EDGE,"E52.sketch_text.stroke-2"),sQuery(id+"F47.wireOp",EDGE,"E52.sketch_text.stroke-3"),sQuery(id+"F47.wireOp",EDGE,"E52.sketch_text.stroke-4"),sQuery(id+"F47.wireOp",EDGE,"E52.sketch_text.stroke-5"),sQuery(id+"F47.wireOp",EDGE,"E52.sketch_text.stroke-6"),sQuery(id+"F47.wireOp",EDGE,"E52.sketch_text.stroke-7"),sQuery(id+"F47.wireOp",EDGE,"E52.sketch_text.stroke-8"),sQuery(id+"F47.wireOp",EDGE,"E52.sketch_text.stroke-9"),sQuery(id+"F47.wireOp",EDGE,"E52.sketch_text.stroke-10"),sQuery(id+"F47.wireOp",EDGE,"E52.sketch_text.stroke-11"),sQuery(id+"F47.wireOp",EDGE,"E52.sketch_text.stroke-12"),sQuery(id+"F47.wireOp",EDGE,"E52.sketch_text.stroke-13"),sQuery(id+"F47.wireOp",EDGE,"E52.sketch_text.stroke-14"),sQuery(id+"F47.wireOp",EDGE,"E52.sketch_text.stroke-15"),sQuery(id+"F47.wireOp",EDGE,"E52.sketch_text.stroke-16"),sQuery(id+"F47.wireOp",EDGE,"E52.sketch_text.stroke-17"),sQuery(id+"F47.wireOp",EDGE,"E52.sketch_text.stroke-18"),sQuery(id+"F47.wireOp",EDGE,"E52.sketch_text.stroke-19"),sQuery(id+"F47.wireOp",EDGE,"E52.sketch_text.stroke-20"),sQuery(id+"F47.wireOp",EDGE,"E52.sketch_text.stroke-21"),sQuery(id+"F47.wireOp",EDGE,"E52.sketch_text.stroke-22"),sQuery(id+"F47.wireOp",EDGE,"E52.sketch_text.stroke-23"),sQuery(id+"F47.wireOp",EDGE,"E52.sketch_text.stroke-24"),sQuery(id+"F47.wireOp",EDGE,"E52.sketch_text.stroke-25"),sQuery(id+"F47.wireOp",EDGE,"E52.sketch_text.stroke-26"),sQuery(id+"F47.wireOp",EDGE,"E52.sketch_text.stroke-27")])]});
            transform(context, id + "F49", {"entities" : qUnion([Q0, Q1]), "transformType" : TransformType.TRANSLATION_3D, "dx" : 0 * mm, "dy" : -15 * mm, "dz" : 0 * mm, "makeCopy" : false});
        }
        {
            var Q0;
            Q0=makeQuery(id+"F48.opExtrude","SWEPT_BODY",BODY,{"disambiguationData":[OSD([sQuery(id+"F47.wireOp",EDGE,"E52.sketch_text.stroke-28"),sQuery(id+"F47.wireOp",EDGE,"E52.sketch_text.stroke-29"),sQuery(id+"F47.wireOp",EDGE,"E52.sketch_text.stroke-30"),sQuery(id+"F47.wireOp",EDGE,"E52.sketch_text.stroke-31"),sQuery(id+"F47.wireOp",EDGE,"E52.sketch_text.stroke-32"),sQuery(id+"F47.wireOp",EDGE,"E52.sketch_text.stroke-33"),sQuery(id+"F47.wireOp",EDGE,"E52.sketch_text.stroke-34"),sQuery(id+"F47.wireOp",EDGE,"E52.sketch_text.stroke-35"),sQuery(id+"F47.wireOp",EDGE,"E52.sketch_text.stroke-36"),sQuery(id+"F47.wireOp",EDGE,"E52.sketch_text.stroke-37")])]});
            var Q1;
            Q1=makeQuery(id+"F48.opExtrude","SWEPT_BODY",BODY,{"disambiguationData":[OSD([sQuery(id+"F47.wireOp",EDGE,"E52.sketch_text.stroke-0"),sQuery(id+"F47.wireOp",EDGE,"E52.sketch_text.stroke-1"),sQuery(id+"F47.wireOp",EDGE,"E52.sketch_text.stroke-2"),sQuery(id+"F47.wireOp",EDGE,"E52.sketch_text.stroke-3"),sQuery(id+"F47.wireOp",EDGE,"E52.sketch_text.stroke-4"),sQuery(id+"F47.wireOp",EDGE,"E52.sketch_text.stroke-5"),sQuery(id+"F47.wireOp",EDGE,"E52.sketch_text.stroke-6"),sQuery(id+"F47.wireOp",EDGE,"E52.sketch_text.stroke-7"),sQuery(id+"F47.wireOp",EDGE,"E52.sketch_text.stroke-8"),sQuery(id+"F47.wireOp",EDGE,"E52.sketch_text.stroke-9"),sQuery(id+"F47.wireOp",EDGE,"E52.sketch_text.stroke-10"),sQuery(id+"F47.wireOp",EDGE,"E52.sketch_text.stroke-11"),sQuery(id+"F47.wireOp",EDGE,"E52.sketch_text.stroke-12"),sQuery(id+"F47.wireOp",EDGE,"E52.sketch_text.stroke-13"),sQuery(id+"F47.wireOp",EDGE,"E52.sketch_text.stroke-14"),sQuery(id+"F47.wireOp",EDGE,"E52.sketch_text.stroke-15"),sQuery(id+"F47.wireOp",EDGE,"E52.sketch_text.stroke-16"),sQuery(id+"F47.wireOp",EDGE,"E52.sketch_text.stroke-17"),sQuery(id+"F47.wireOp",EDGE,"E52.sketch_text.stroke-18"),sQuery(id+"F47.wireOp",EDGE,"E52.sketch_text.stroke-19"),sQuery(id+"F47.wireOp",EDGE,"E52.sketch_text.stroke-20"),sQuery(id+"F47.wireOp",EDGE,"E52.sketch_text.stroke-21"),sQuery(id+"F47.wireOp",EDGE,"E52.sketch_text.stroke-22"),sQuery(id+"F47.wireOp",EDGE,"E52.sketch_text.stroke-23"),sQuery(id+"F47.wireOp",EDGE,"E52.sketch_text.stroke-24"),sQuery(id+"F47.wireOp",EDGE,"E52.sketch_text.stroke-25"),sQuery(id+"F47.wireOp",EDGE,"E52.sketch_text.stroke-26"),sQuery(id+"F47.wireOp",EDGE,"E52.sketch_text.stroke-27")])]});
            transform(context, id + "F50", {"entities" : qUnion([Q0, Q1]), "transformType" : TransformType.TRANSLATION_3D, "dx" : 0 * mm, "dy" : 0 * mm, "dz" : -1 * mm, "makeCopy" : false});
        }
        {
            var Q0;
            Q0=makeQuery(id+"F48.opExtrude","SWEPT_BODY",BODY,{"disambiguationData":[OSD([sQuery(id+"F47.wireOp",EDGE,"E52.sketch_text.stroke-28"),sQuery(id+"F47.wireOp",EDGE,"E52.sketch_text.stroke-29"),sQuery(id+"F47.wireOp",EDGE,"E52.sketch_text.stroke-30"),sQuery(id+"F47.wireOp",EDGE,"E52.sketch_text.stroke-31"),sQuery(id+"F47.wireOp",EDGE,"E52.sketch_text.stroke-32"),sQuery(id+"F47.wireOp",EDGE,"E52.sketch_text.stroke-33"),sQuery(id+"F47.wireOp",EDGE,"E52.sketch_text.stroke-34"),sQuery(id+"F47.wireOp",EDGE,"E52.sketch_text.stroke-35"),sQuery(id+"F47.wireOp",EDGE,"E52.sketch_text.stroke-36"),sQuery(id+"F47.wireOp",EDGE,"E52.sketch_text.stroke-37")])]});
            var Q1;
            Q1=makeQuery(id+"F48.opExtrude","SWEPT_BODY",BODY,{"disambiguationData":[OSD([sQuery(id+"F47.wireOp",EDGE,"E52.sketch_text.stroke-0"),sQuery(id+"F47.wireOp",EDGE,"E52.sketch_text.stroke-1"),sQuery(id+"F47.wireOp",EDGE,"E52.sketch_text.stroke-2"),sQuery(id+"F47.wireOp",EDGE,"E52.sketch_text.stroke-3"),sQuery(id+"F47.wireOp",EDGE,"E52.sketch_text.stroke-4"),sQuery(id+"F47.wireOp",EDGE,"E52.sketch_text.stroke-5"),sQuery(id+"F47.wireOp",EDGE,"E52.sketch_text.stroke-6"),sQuery(id+"F47.wireOp",EDGE,"E52.sketch_text.stroke-7"),sQuery(id+"F47.wireOp",EDGE,"E52.sketch_text.stroke-8"),sQuery(id+"F47.wireOp",EDGE,"E52.sketch_text.stroke-9"),sQuery(id+"F47.wireOp",EDGE,"E52.sketch_text.stroke-10"),sQuery(id+"F47.wireOp",EDGE,"E52.sketch_text.stroke-11"),sQuery(id+"F47.wireOp",EDGE,"E52.sketch_text.stroke-12"),sQuery(id+"F47.wireOp",EDGE,"E52.sketch_text.stroke-13"),sQuery(id+"F47.wireOp",EDGE,"E52.sketch_text.stroke-14"),sQuery(id+"F47.wireOp",EDGE,"E52.sketch_text.stroke-15"),sQuery(id+"F47.wireOp",EDGE,"E52.sketch_text.stroke-16"),sQuery(id+"F47.wireOp",EDGE,"E52.sketch_text.stroke-17"),sQuery(id+"F47.wireOp",EDGE,"E52.sketch_text.stroke-18"),sQuery(id+"F47.wireOp",EDGE,"E52.sketch_text.stroke-19"),sQuery(id+"F47.wireOp",EDGE,"E52.sketch_text.stroke-20"),sQuery(id+"F47.wireOp",EDGE,"E52.sketch_text.stroke-21"),sQuery(id+"F47.wireOp",EDGE,"E52.sketch_text.stroke-22"),sQuery(id+"F47.wireOp",EDGE,"E52.sketch_text.stroke-23"),sQuery(id+"F47.wireOp",EDGE,"E52.sketch_text.stroke-24"),sQuery(id+"F47.wireOp",EDGE,"E52.sketch_text.stroke-25"),sQuery(id+"F47.wireOp",EDGE,"E52.sketch_text.stroke-26"),sQuery(id+"F47.wireOp",EDGE,"E52.sketch_text.stroke-27")])]});
            deleteBodies(context, id + "F51", {"entities" : qUnion([Q0, Q1])});
        }
        {
            var Q0;
            Q0=makeQuery(id+"F30.opExtrude","SWEPT_BODY",BODY,{"disambiguationData":[OSD([sQuery(id+"F29.wireOp",EDGE,"E40"),sQuery(id+"F29.wireOp",EDGE,"E41"),sQuery(id+"F29.wireOp",EDGE,"E42"),sQuery(id+"F29.wireOp",EDGE,"E43"),sQuery(id+"F29.wireOp",EDGE,"E44"),sQuery(id+"F29.wireOp",EDGE,"E45")])]});
            var Q1;
            Q1=makeQuery(id+"F31.opPattern","COPY",BODY,{"derivedFrom":makeQuery(id+"F30.opExtrude","SWEPT_BODY",BODY,{"disambiguationData":[OSD([sQuery(id+"F29.wireOp",EDGE,"E40"),sQuery(id+"F29.wireOp",EDGE,"E41"),sQuery(id+"F29.wireOp",EDGE,"E42"),sQuery(id+"F29.wireOp",EDGE,"E43"),sQuery(id+"F29.wireOp",EDGE,"E44"),sQuery(id+"F29.wireOp",EDGE,"E45")])]}),"instanceName":"1"});
            var Q2;
            Q2=makeQuery(id+"F1.opExtrude","SWEPT_BODY",BODY,{"disambiguationData":[OSD([sQuery(id+"F0.wireOp",EDGE,"E0.bottom"),sQuery(id+"F0.wireOp",EDGE,"E0.top"),sQuery(id+"F0.wireOp",EDGE,"E0.left"),sQuery(id+"F0.wireOp",EDGE,"E0.right"),sQuery(id+"F0.wireOp",EDGE,"E2"),sQuery(id+"F0.wireOp",EDGE,"E3"),sQuery(id+"F0.wireOp",EDGE,"E4"),sQuery(id+"F0.wireOp",EDGE,"E5"),sQuery(id+"F0.wireOp",EDGE,"E6.trimOffspring")])]});
            booleanBodies(context, id + "F52", {"operationType" : BooleanOperationType.UNION, "tools" : qUnion([Q0, Q1, Q2])});
        }
        {
            var Q0;
            Q0=makeQuery(id+"F1.opExtrude","SWEPT_EDGE",EDGE,{"disambiguationData":[OSD([sQuery(id+"F0.wireOp",EDGE,"E0.top"),sQuery(id+"F0.wireOp",EDGE,"E0.right")])]});
            var Q1;
            Q1=makeQuery(id+"F1.opExtrude","SWEPT_EDGE",EDGE,{"disambiguationData":[OSD([sQuery(id+"F0.wireOp",EDGE,"E0.top"),sQuery(id+"F0.wireOp",EDGE,"E0.left")])]});
            var Q2;
            Q2=makeQuery(id+"F1.opExtrude","SWEPT_EDGE",EDGE,{"disambiguationData":[OSD([sQuery(id+"F0.wireOp",EDGE,"E3"),sQuery(id+"F0.wireOp",EDGE,"E4")])]});
            var Q3;
            Q3=makeQuery(id+"F1.opExtrude","SWEPT_EDGE",EDGE,{"disambiguationData":[OSD([sQuery(id+"F0.wireOp",EDGE,"E2"),sQuery(id+"F0.wireOp",EDGE,"E5")])]});
            fillet(context, id + "F53", {"entities" : qUnion([Q0, Q1, Q2, Q3]), "radius" : 5 * mm, "tangentPropagation" : true, "allowEdgeOverflow" : false});
        }
        {
            var Q0;
            {var subQ0=sQuery(id+"F0.wireOp",EDGE,"E3");var subQ1=sQuery(id+"F0.wireOp",EDGE,"E2");var subQ2=sQuery(id+"F0.wireOp",EDGE,"E0.right");var subQ3=sQuery(id+"F0.wireOp",EDGE,"E0.left");var subQ4=sQuery(id+"F0.wireOp",EDGE,"E0.top");var subQ5=sQuery(id+"F0.wireOp",EDGE,"E4");var subQ6=sQuery(id+"F0.wireOp",EDGE,"E5");Q0=makeQuery(id+"F52.opBoolean","INTERSECT",EDGE,{"derivedFrom":[makeQuery(id+"F30.opExtrude","SWEPT_FACE",FACE,{"disambiguationData":[OSD([sQuery(id+"F29.wireOp",EDGE,"E44")])]}),makeQuery(id+"F12.opBoolean","SPLIT",FACE,{"disambiguationData":[TD([makeQuery(id+"F1.opExtrude","SWEPT_FACE",FACE,{"disambiguationData":[OSD([subQ4])]})])],"derivedFrom":makeQuery(id+"F1.opExtrude","CAP_FACE",FACE,{"disambiguationData":[OSD([sQuery(id+"F0.wireOp",EDGE,"E0.bottom"),subQ4,subQ3,subQ2,subQ1,subQ0,subQ5,subQ6,sQuery(id+"F0.wireOp",EDGE,"E6.trimOffspring")])],"isStart":false})})]});}
            var Q1;
            {var subQ0=sQuery(id+"F0.wireOp",EDGE,"E3");var subQ1=sQuery(id+"F0.wireOp",EDGE,"E2");var subQ2=sQuery(id+"F0.wireOp",EDGE,"E0.right");var subQ3=sQuery(id+"F0.wireOp",EDGE,"E0.left");var subQ4=sQuery(id+"F0.wireOp",EDGE,"E0.top");var subQ5=sQuery(id+"F0.wireOp",EDGE,"E4");var subQ6=sQuery(id+"F0.wireOp",EDGE,"E5");Q1=makeQuery(id+"F52.opBoolean","INTERSECT",EDGE,{"derivedFrom":[makeQuery(id+"F30.opExtrude","SWEPT_FACE",FACE,{"disambiguationData":[OSD([sQuery(id+"F29.wireOp",EDGE,"E42")])]}),makeQuery(id+"F12.opBoolean","SPLIT",FACE,{"disambiguationData":[TD([makeQuery(id+"F1.opExtrude","SWEPT_FACE",FACE,{"disambiguationData":[OSD([subQ4])]})])],"derivedFrom":makeQuery(id+"F1.opExtrude","CAP_FACE",FACE,{"disambiguationData":[OSD([sQuery(id+"F0.wireOp",EDGE,"E0.bottom"),subQ4,subQ3,subQ2,subQ1,subQ0,subQ5,subQ6,sQuery(id+"F0.wireOp",EDGE,"E6.trimOffspring")])],"isStart":false})})]});}
            var Q2;
            {var subQ0=sQuery(id+"F0.wireOp",EDGE,"E3");var subQ1=sQuery(id+"F0.wireOp",EDGE,"E2");var subQ2=sQuery(id+"F0.wireOp",EDGE,"E0.right");var subQ3=sQuery(id+"F0.wireOp",EDGE,"E0.left");var subQ4=sQuery(id+"F0.wireOp",EDGE,"E0.top");var subQ5=sQuery(id+"F0.wireOp",EDGE,"E4");var subQ6=sQuery(id+"F0.wireOp",EDGE,"E5");Q2=makeQuery(id+"F52.opBoolean","INTERSECT",EDGE,{"derivedFrom":[makeQuery(id+"F31.opPattern","COPY",FACE,{"derivedFrom":makeQuery(id+"F30.opExtrude","SWEPT_FACE",FACE,{"disambiguationData":[OSD([sQuery(id+"F29.wireOp",EDGE,"E44")])]}),"instanceName":"1"}),makeQuery(id+"F12.opBoolean","SPLIT",FACE,{"disambiguationData":[TD([makeQuery(id+"F1.opExtrude","SWEPT_FACE",FACE,{"disambiguationData":[OSD([subQ4])]})])],"derivedFrom":makeQuery(id+"F1.opExtrude","CAP_FACE",FACE,{"disambiguationData":[OSD([sQuery(id+"F0.wireOp",EDGE,"E0.bottom"),subQ4,subQ3,subQ2,subQ1,subQ0,subQ5,subQ6,sQuery(id+"F0.wireOp",EDGE,"E6.trimOffspring")])],"isStart":false})})]});}
            var Q3;
            {var subQ0=sQuery(id+"F0.wireOp",EDGE,"E3");var subQ1=sQuery(id+"F0.wireOp",EDGE,"E2");var subQ2=sQuery(id+"F0.wireOp",EDGE,"E0.right");var subQ3=sQuery(id+"F0.wireOp",EDGE,"E0.left");var subQ4=sQuery(id+"F0.wireOp",EDGE,"E0.top");var subQ5=sQuery(id+"F0.wireOp",EDGE,"E4");var subQ6=sQuery(id+"F0.wireOp",EDGE,"E5");Q3=makeQuery(id+"F52.opBoolean","INTERSECT",EDGE,{"derivedFrom":[makeQuery(id+"F31.opPattern","COPY",FACE,{"derivedFrom":makeQuery(id+"F30.opExtrude","SWEPT_FACE",FACE,{"disambiguationData":[OSD([sQuery(id+"F29.wireOp",EDGE,"E42")])]}),"instanceName":"1"}),makeQuery(id+"F12.opBoolean","SPLIT",FACE,{"disambiguationData":[TD([makeQuery(id+"F1.opExtrude","SWEPT_FACE",FACE,{"disambiguationData":[OSD([subQ4])]})])],"derivedFrom":makeQuery(id+"F1.opExtrude","CAP_FACE",FACE,{"disambiguationData":[OSD([sQuery(id+"F0.wireOp",EDGE,"E0.bottom"),subQ4,subQ3,subQ2,subQ1,subQ0,subQ5,subQ6,sQuery(id+"F0.wireOp",EDGE,"E6.trimOffspring")])],"isStart":false})})]});}
            var Q4;
            {var subQ0=sQuery(id+"F0.wireOp",EDGE,"E3");var subQ1=sQuery(id+"F0.wireOp",EDGE,"E2");var subQ2=sQuery(id+"F0.wireOp",EDGE,"E0.right");var subQ3=sQuery(id+"F0.wireOp",EDGE,"E0.left");var subQ4=sQuery(id+"F0.wireOp",EDGE,"E0.top");var subQ5=sQuery(id+"F0.wireOp",EDGE,"E4");var subQ6=sQuery(id+"F0.wireOp",EDGE,"E5");Q4=makeQuery(id+"F52.opBoolean","INTERSECT",EDGE,{"derivedFrom":[makeQuery(id+"F31.opPattern","COPY",FACE,{"derivedFrom":makeQuery(id+"F30.opExtrude","CAP_FACE",FACE,{"disambiguationData":[OSD([sQuery(id+"F29.wireOp",EDGE,"E40"),sQuery(id+"F29.wireOp",EDGE,"E41"),sQuery(id+"F29.wireOp",EDGE,"E42"),sQuery(id+"F29.wireOp",EDGE,"E43"),sQuery(id+"F29.wireOp",EDGE,"E44"),sQuery(id+"F29.wireOp",EDGE,"E45")])],"isStart":true}),"instanceName":"1"}),makeQuery(id+"F12.opBoolean","SPLIT",FACE,{"disambiguationData":[TD([makeQuery(id+"F1.opExtrude","SWEPT_FACE",FACE,{"disambiguationData":[OSD([subQ4])]})])],"derivedFrom":makeQuery(id+"F1.opExtrude","CAP_FACE",FACE,{"disambiguationData":[OSD([sQuery(id+"F0.wireOp",EDGE,"E0.bottom"),subQ4,subQ3,subQ2,subQ1,subQ0,subQ5,subQ6,sQuery(id+"F0.wireOp",EDGE,"E6.trimOffspring")])],"isStart":false})})]});}
            var Q5;
            {var subQ0=sQuery(id+"F0.wireOp",EDGE,"E3");var subQ1=sQuery(id+"F0.wireOp",EDGE,"E2");var subQ2=sQuery(id+"F0.wireOp",EDGE,"E0.right");var subQ3=sQuery(id+"F0.wireOp",EDGE,"E0.left");var subQ4=sQuery(id+"F0.wireOp",EDGE,"E0.top");var subQ5=sQuery(id+"F0.wireOp",EDGE,"E4");var subQ6=sQuery(id+"F0.wireOp",EDGE,"E5");Q5=makeQuery(id+"F52.opBoolean","INTERSECT",EDGE,{"derivedFrom":[makeQuery(id+"F30.opExtrude","CAP_FACE",FACE,{"disambiguationData":[OSD([sQuery(id+"F29.wireOp",EDGE,"E40"),sQuery(id+"F29.wireOp",EDGE,"E41"),sQuery(id+"F29.wireOp",EDGE,"E42"),sQuery(id+"F29.wireOp",EDGE,"E43"),sQuery(id+"F29.wireOp",EDGE,"E44"),sQuery(id+"F29.wireOp",EDGE,"E45")])],"isStart":false}),makeQuery(id+"F12.opBoolean","SPLIT",FACE,{"disambiguationData":[TD([makeQuery(id+"F1.opExtrude","SWEPT_FACE",FACE,{"disambiguationData":[OSD([subQ4])]})])],"derivedFrom":makeQuery(id+"F1.opExtrude","CAP_FACE",FACE,{"disambiguationData":[OSD([sQuery(id+"F0.wireOp",EDGE,"E0.bottom"),subQ4,subQ3,subQ2,subQ1,subQ0,subQ5,subQ6,sQuery(id+"F0.wireOp",EDGE,"E6.trimOffspring")])],"isStart":false})})]});}
            fillet(context, id + "F54", {"entities" : qUnion([Q0, Q1, Q2, Q3, Q4, Q5]), "radius" : 2 * mm, "tangentPropagation" : true, "allowEdgeOverflow" : false});
        }
        {
            var Q0;
            {var subQ0=sQuery(id+"F0.wireOp",EDGE,"E3");var subQ1=sQuery(id+"F0.wireOp",EDGE,"E2");var subQ2=sQuery(id+"F0.wireOp",EDGE,"E0.right");var subQ3=sQuery(id+"F0.wireOp",EDGE,"E0.left");var subQ4=sQuery(id+"F0.wireOp",EDGE,"E0.top");var subQ5=sQuery(id+"F0.wireOp",EDGE,"E4");var subQ6=sQuery(id+"F0.wireOp",EDGE,"E5");Q0=makeQuery(id+"F53.opFillet","BLEND_EDGE",EDGE,{"blendedFrom":[makeQuery(id+"F1.opExtrude","SWEPT_EDGE",EDGE,{"disambiguationData":[OSD([subQ4,subQ2])]}),makeQuery(id+"F12.opBoolean","SPLIT",FACE,{"disambiguationData":[TD([makeQuery(id+"F1.opExtrude","SWEPT_FACE",FACE,{"disambiguationData":[OSD([subQ4])]})])],"derivedFrom":makeQuery(id+"F1.opExtrude","CAP_FACE",FACE,{"disambiguationData":[OSD([sQuery(id+"F0.wireOp",EDGE,"E0.bottom"),subQ4,subQ3,subQ2,subQ1,subQ0,subQ5,subQ6,sQuery(id+"F0.wireOp",EDGE,"E6.trimOffspring")])],"isStart":false})})],"blendedInto":[makeQuery(id+"F12.opBoolean","SPLIT",FACE,{"disambiguationData":[TD([makeQuery(id+"F1.opExtrude","SWEPT_FACE",FACE,{"disambiguationData":[OSD([subQ4])]})])],"derivedFrom":makeQuery(id+"F1.opExtrude","CAP_FACE",FACE,{"disambiguationData":[OSD([sQuery(id+"F0.wireOp",EDGE,"E0.bottom"),subQ4,subQ3,subQ2,subQ1,subQ0,subQ5,subQ6,sQuery(id+"F0.wireOp",EDGE,"E6.trimOffspring")])],"isStart":false})})]});}
            fillet(context, id + "F55", {"entities" : qUnion([Q0]), "radius" : 2 * mm, "tangentPropagation" : true, "allowEdgeOverflow" : false});
        }
        {
            var Q0;
            Q0=makeQuery(id+"F17.opExtrude","SWEPT_EDGE",EDGE,{"disambiguationData":[OSD([sQuery(id+"F16.wireOp",EDGE,"E11.top"),sQuery(id+"F16.wireOp",EDGE,"E11.right")])]});
            var Q1;
            Q1=makeQuery(id+"F17.opExtrude","SWEPT_EDGE",EDGE,{"disambiguationData":[OSD([sQuery(id+"F16.wireOp",EDGE,"E11.top"),sQuery(id+"F16.wireOp",EDGE,"E11.left")])]});
            fillet(context, id + "F56", {"entities" : qUnion([Q0, Q1]), "radius" : 5 * mm, "tangentPropagation" : true, "allowEdgeOverflow" : false});
        }
        {
            var Q0;
            Q0=makeQuery(id+"F17.opExtrude","CAP_EDGE",EDGE,{"disambiguationData":[OSD([sQuery(id+"F16.wireOp",EDGE,"E11.top")])],"isStart":false});
            var Q1;
            {var subQ1=sQuery(id+"F16.wireOp",EDGE,"E11.right");var subQ2=sQuery(id+"F16.wireOp",EDGE,"E11.bottom");Q1=makeQuery(id+"F39.opBoolean","SPLIT",EDGE,{"disambiguationData":[TD([makeQuery(id+"F17.opExtrude","SWEPT_FACE",FACE,{"disambiguationData":[OSD([subQ2])]})])],"derivedFrom":makeQuery(id+"F17.opExtrude","CAP_EDGE",EDGE,{"disambiguationData":[OSD([subQ1])],"isStart":false})});}
            var Q2;
            {var subQ0=sQuery(id+"F16.wireOp",EDGE,"E11.bottom");var subQ1=sQuery(id+"F16.wireOp",EDGE,"E11.right");Q2=makeQuery(id+"F20.opBoolean","SPLIT",EDGE,{"disambiguationData":[TD([makeQuery(id+"F17.opExtrude","SWEPT_FACE",FACE,{"disambiguationData":[OSD([subQ1])]})])],"derivedFrom":makeQuery(id+"F17.opExtrude","CAP_EDGE",EDGE,{"disambiguationData":[OSD([subQ0])],"isStart":false})});}
            var Q3;
            Q3=makeQuery(id+"F39.opBoolean","INTERSECT",EDGE,{"derivedFrom":[makeQuery(id+"F28.opBoolean","MERGE",FACE,{"derivedFrom":[makeQuery(id+"F17.opExtrude","SWEPT_FACE",FACE,{"disambiguationData":[OSD([sQuery(id+"F16.wireOp",EDGE,"E11.right")])]}),makeQuery(id+"F24.opBoolean","COPY",FACE,{"derivedFrom":makeQuery(id+"F23.opExtrude","SWEPT_FACE",FACE,{"disambiguationData":[OSD([sQuery(id+"F22.wireOp",EDGE,"E30")])]})})]}),makeQuery(id+"F35.opExtrude","SWEPT_FACE",FACE,{"disambiguationData":[OSD([sQuery(id+"F34.wireOp",EDGE,"E46.top")])]})]});
            var Q4;
            Q4=makeQuery(id+"F39.opBoolean","INTERSECT",EDGE,{"derivedFrom":[makeQuery(id+"F28.opBoolean","MERGE",FACE,{"derivedFrom":[makeQuery(id+"F17.opExtrude","SWEPT_FACE",FACE,{"disambiguationData":[OSD([sQuery(id+"F16.wireOp",EDGE,"E11.right")])]}),makeQuery(id+"F24.opBoolean","COPY",FACE,{"derivedFrom":makeQuery(id+"F23.opExtrude","SWEPT_FACE",FACE,{"disambiguationData":[OSD([sQuery(id+"F22.wireOp",EDGE,"E30")])]})})]}),makeQuery(id+"F35.opExtrude","SWEPT_FACE",FACE,{"disambiguationData":[OSD([sQuery(id+"F34.wireOp",EDGE,"E46.bottom")])]})]});
            var Q5;
            {var subQ0=sQuery(id+"F16.wireOp",EDGE,"E11.bottom");var subQ1=sQuery(id+"F16.wireOp",EDGE,"E11.left");Q5=makeQuery(id+"F20.opBoolean","SPLIT",EDGE,{"disambiguationData":[TD([makeQuery(id+"F17.opExtrude","SWEPT_FACE",FACE,{"disambiguationData":[OSD([subQ1])]})])],"derivedFrom":makeQuery(id+"F17.opExtrude","CAP_EDGE",EDGE,{"disambiguationData":[OSD([subQ0])],"isStart":false})});}
            var Q6;
            {var subQ1=sQuery(id+"F16.wireOp",EDGE,"E11.left");var subQ2=sQuery(id+"F16.wireOp",EDGE,"E11.bottom");Q6=makeQuery(id+"F39.opBoolean","SPLIT",EDGE,{"disambiguationData":[TD([makeQuery(id+"F17.opExtrude","SWEPT_FACE",FACE,{"disambiguationData":[OSD([subQ2])]})])],"derivedFrom":makeQuery(id+"F17.opExtrude","CAP_EDGE",EDGE,{"disambiguationData":[OSD([subQ1])],"isStart":false})});}
            var Q7;
            Q7=makeQuery(id+"F39.opBoolean","INTERSECT",EDGE,{"derivedFrom":[makeQuery(id+"F28.opBoolean","MERGE",FACE,{"derivedFrom":[makeQuery(id+"F17.opExtrude","SWEPT_FACE",FACE,{"disambiguationData":[OSD([sQuery(id+"F16.wireOp",EDGE,"E11.left")])]}),makeQuery(id+"F24.opBoolean","COPY",FACE,{"derivedFrom":makeQuery(id+"F23.opExtrude","SWEPT_FACE",FACE,{"disambiguationData":[OSD([sQuery(id+"F22.wireOp",EDGE,"E25")])]})})]}),makeQuery(id+"F36.opPattern","COPY",FACE,{"derivedFrom":makeQuery(id+"F35.opExtrude","SWEPT_FACE",FACE,{"disambiguationData":[OSD([sQuery(id+"F34.wireOp",EDGE,"E46.top")])]}),"instanceName":"1"})]});
            var Q8;
            Q8=makeQuery(id+"F39.opBoolean","INTERSECT",EDGE,{"derivedFrom":[makeQuery(id+"F28.opBoolean","MERGE",FACE,{"derivedFrom":[makeQuery(id+"F17.opExtrude","SWEPT_FACE",FACE,{"disambiguationData":[OSD([sQuery(id+"F16.wireOp",EDGE,"E11.left")])]}),makeQuery(id+"F24.opBoolean","COPY",FACE,{"derivedFrom":makeQuery(id+"F23.opExtrude","SWEPT_FACE",FACE,{"disambiguationData":[OSD([sQuery(id+"F22.wireOp",EDGE,"E25")])]})})]}),makeQuery(id+"F36.opPattern","COPY",FACE,{"derivedFrom":makeQuery(id+"F35.opExtrude","SWEPT_FACE",FACE,{"disambiguationData":[OSD([sQuery(id+"F34.wireOp",EDGE,"E46.bottom")])]}),"instanceName":"1"})]});
            var Q9;
            Q9=makeQuery(id+"F20.opBoolean","INTERSECT",EDGE,{"derivedFrom":[makeQuery(id+"F17.opExtrude","CAP_FACE",FACE,{"disambiguationData":[OSD([sQuery(id+"F16.wireOp",EDGE,"E11.bottom"),sQuery(id+"F16.wireOp",EDGE,"E11.top"),sQuery(id+"F16.wireOp",EDGE,"E11.left"),sQuery(id+"F16.wireOp",EDGE,"E11.right")])],"isStart":false}),makeQuery(id+"F19.opExtrude","SWEPT_FACE",FACE,{"disambiguationData":[OSD([sQuery(id+"F18.wireOp",EDGE,"E13"),sQuery(id+"F18.wireOp",EDGE,"E17")])]})]});
            var Q10;
            Q10=makeQuery(id+"F20.opBoolean","INTERSECT",EDGE,{"derivedFrom":[makeQuery(id+"F17.opExtrude","CAP_FACE",FACE,{"disambiguationData":[OSD([sQuery(id+"F16.wireOp",EDGE,"E11.bottom"),sQuery(id+"F16.wireOp",EDGE,"E11.top"),sQuery(id+"F16.wireOp",EDGE,"E11.left"),sQuery(id+"F16.wireOp",EDGE,"E11.right")])],"isStart":false}),makeQuery(id+"F19.opExtrude","SWEPT_FACE",FACE,{"disambiguationData":[OSD([sQuery(id+"F18.wireOp",EDGE,"E14")])]})]});
            var Q11;
            Q11=makeQuery(id+"F20.opBoolean","INTERSECT",EDGE,{"derivedFrom":[makeQuery(id+"F17.opExtrude","CAP_FACE",FACE,{"disambiguationData":[OSD([sQuery(id+"F16.wireOp",EDGE,"E11.bottom"),sQuery(id+"F16.wireOp",EDGE,"E11.top"),sQuery(id+"F16.wireOp",EDGE,"E11.left"),sQuery(id+"F16.wireOp",EDGE,"E11.right")])],"isStart":false}),makeQuery(id+"F19.opExtrude","SWEPT_FACE",FACE,{"disambiguationData":[OSD([sQuery(id+"F18.wireOp",EDGE,"E16")])]})]});
            var Q12;
            Q12=makeQuery(id+"F28.opBoolean","MERGE",EDGE,{"derivedFrom":[makeQuery(id+"F17.opExtrude","SWEPT_EDGE",EDGE,{"disambiguationData":[OSD([sQuery(id+"F16.wireOp",EDGE,"E11.bottom"),sQuery(id+"F16.wireOp",EDGE,"E11.right")])]}),makeQuery(id+"F27.opBoolean","COPY",EDGE,{"derivedFrom":makeQuery(id+"F26.opExtrude","SWEPT_EDGE",EDGE,{"disambiguationData":[OSD([sQuery(id+"F25.wireOp",EDGE,"E38"),sQuery(id+"F25.wireOp",EDGE,"E39")])]})})]});
            var Q13;
            Q13=makeQuery(id+"F28.opBoolean","MERGE",EDGE,{"derivedFrom":[makeQuery(id+"F20.opBoolean","COPY",EDGE,{"derivedFrom":makeQuery(id+"F19.opExtrude","SWEPT_EDGE",EDGE,{"disambiguationData":[OSD([sQuery(id+"F18.wireOp",EDGE,"E14"),sQuery(id+"F18.wireOp",EDGE,"E15")])]})}),makeQuery(id+"F27.opBoolean","INTERSECT",EDGE,{"derivedFrom":[makeQuery(id+"F24.opBoolean","COPY",FACE,{"derivedFrom":makeQuery(id+"F23.opExtrude","SWEPT_FACE",FACE,{"disambiguationData":[OSD([sQuery(id+"F22.wireOp",EDGE,"E20")])]})}),makeQuery(id+"F26.opExtrude","SWEPT_FACE",FACE,{"disambiguationData":[OSD([sQuery(id+"F25.wireOp",EDGE,"E39")])]})]})]});
            var Q14;
            Q14=makeQuery(id+"F28.opBoolean","MERGE",EDGE,{"derivedFrom":[makeQuery(id+"F20.opBoolean","COPY",EDGE,{"derivedFrom":makeQuery(id+"F19.opExtrude","SWEPT_EDGE",EDGE,{"disambiguationData":[OSD([sQuery(id+"F18.wireOp",EDGE,"E15"),sQuery(id+"F18.wireOp",EDGE,"E16")])]})}),makeQuery(id+"F27.opBoolean","INTERSECT",EDGE,{"derivedFrom":[makeQuery(id+"F24.opBoolean","COPY",FACE,{"derivedFrom":makeQuery(id+"F23.opExtrude","SWEPT_FACE",FACE,{"disambiguationData":[OSD([sQuery(id+"F22.wireOp",EDGE,"E22")])]})}),makeQuery(id+"F26.opExtrude","SWEPT_FACE",FACE,{"disambiguationData":[OSD([sQuery(id+"F25.wireOp",EDGE,"E39")])]})]})]});
            var Q15;
            Q15=makeQuery(id+"F28.opBoolean","MERGE",EDGE,{"derivedFrom":[makeQuery(id+"F17.opExtrude","SWEPT_EDGE",EDGE,{"disambiguationData":[OSD([sQuery(id+"F16.wireOp",EDGE,"E11.bottom"),sQuery(id+"F16.wireOp",EDGE,"E11.left")])]}),makeQuery(id+"F27.opBoolean","COPY",EDGE,{"derivedFrom":makeQuery(id+"F26.opExtrude","SWEPT_EDGE",EDGE,{"disambiguationData":[OSD([sQuery(id+"F25.wireOp",EDGE,"E36"),sQuery(id+"F25.wireOp",EDGE,"E39")])]})})]});
            fillet(context, id + "F57", {"entities" : qUnion([Q0, Q1, Q2, Q3, Q4, Q5, Q6, Q7, Q8, Q9, Q10, Q11, Q12, Q13, Q14, Q15]), "radius" : 2 * mm, "tangentPropagation" : true, "allowEdgeOverflow" : false});
        }
        {
            var Q0;
            Q0=makeQuery(id+"F39.opBoolean","INTERSECT",EDGE,{"derivedFrom":[makeQuery(id+"F17.opExtrude","CAP_FACE",FACE,{"disambiguationData":[OSD([sQuery(id+"F16.wireOp",EDGE,"E11.bottom"),sQuery(id+"F16.wireOp",EDGE,"E11.top"),sQuery(id+"F16.wireOp",EDGE,"E11.left"),sQuery(id+"F16.wireOp",EDGE,"E11.right")])],"isStart":false}),makeQuery(id+"F35.opExtrude","SWEPT_FACE",FACE,{"disambiguationData":[OSD([sQuery(id+"F34.wireOp",EDGE,"E46.left")])]})]});
            var Q1;
            Q1=makeQuery(id+"F39.opBoolean","INTERSECT",EDGE,{"derivedFrom":[makeQuery(id+"F17.opExtrude","CAP_FACE",FACE,{"disambiguationData":[OSD([sQuery(id+"F16.wireOp",EDGE,"E11.bottom"),sQuery(id+"F16.wireOp",EDGE,"E11.top"),sQuery(id+"F16.wireOp",EDGE,"E11.left"),sQuery(id+"F16.wireOp",EDGE,"E11.right")])],"isStart":false}),makeQuery(id+"F36.opPattern","COPY",FACE,{"derivedFrom":makeQuery(id+"F35.opExtrude","SWEPT_FACE",FACE,{"disambiguationData":[OSD([sQuery(id+"F34.wireOp",EDGE,"E46.right")])]}),"instanceName":"1"})]});
            fillet(context, id + "F58", {"entities" : qUnion([Q0, Q1]), "radius" : 0.8 * mm, "tangentPropagation" : true, "allowEdgeOverflow" : false});
        }
        {
            var Q0;
            {var subQ0=sQuery(id+"F16.wireOp",EDGE,"E11.left");var subQ1=sQuery(id+"F16.wireOp",EDGE,"E11.top");var subQ2=sQuery(id+"F16.wireOp",EDGE,"E11.right");Q0=makeQuery(id+"F56.opFillet","BLEND_EDGE",EDGE,{"blendedFrom":[makeQuery(id+"F17.opExtrude","SWEPT_EDGE",EDGE,{"disambiguationData":[OSD([subQ1,subQ2])]}),makeQuery(id+"F28.opBoolean","SPLIT",FACE,{"disambiguationData":[TD([makeQuery(id+"F5.opPattern","COPY",FACE,{"derivedFrom":makeQuery(id+"F3.opExtrude","SWEPT_FACE",FACE,{"disambiguationData":[OSD([sQuery(id+"F2.wireOp",EDGE,"E7.1")])]}),"instanceName":"1"})])],"derivedFrom":makeQuery(id+"F17.opExtrude","CAP_FACE",FACE,{"disambiguationData":[OSD([sQuery(id+"F16.wireOp",EDGE,"E11.bottom"),subQ1,subQ0,subQ2])],"isStart":true})})],"blendedInto":[makeQuery(id+"F28.opBoolean","SPLIT",FACE,{"disambiguationData":[TD([makeQuery(id+"F5.opPattern","COPY",FACE,{"derivedFrom":makeQuery(id+"F3.opExtrude","SWEPT_FACE",FACE,{"disambiguationData":[OSD([sQuery(id+"F2.wireOp",EDGE,"E7.1")])]}),"instanceName":"1"})])],"derivedFrom":makeQuery(id+"F17.opExtrude","CAP_FACE",FACE,{"disambiguationData":[OSD([sQuery(id+"F16.wireOp",EDGE,"E11.bottom"),subQ1,subQ0,subQ2])],"isStart":true})})]});}
            var Q1;
            {var subQ1=sQuery(id+"F16.wireOp",EDGE,"E11.right");var subQ5=makeQuery(id+"F5.opPattern","COPY",FACE,{"derivedFrom":makeQuery(id+"F3.opExtrude","SWEPT_FACE",FACE,{"disambiguationData":[OSD([sQuery(id+"F2.wireOp",EDGE,"E7.1")])]}),"instanceName":"1"});Q1=makeQuery(id+"F39.opBoolean","SPLIT",EDGE,{"disambiguationData":[TD([subQ5])],"derivedFrom":makeQuery(id+"F28.opBoolean","SPLIT",EDGE,{"disambiguationData":[TD([subQ5])],"derivedFrom":makeQuery(id+"F17.opExtrude","CAP_EDGE",EDGE,{"disambiguationData":[OSD([subQ1])],"isStart":true})})});}
            var Q2;
            {var subQ1=sQuery(id+"F16.wireOp",EDGE,"E11.left");var subQ5=makeQuery(id+"F5.opPattern","COPY",FACE,{"derivedFrom":makeQuery(id+"F3.opExtrude","SWEPT_FACE",FACE,{"disambiguationData":[OSD([sQuery(id+"F2.wireOp",EDGE,"E7.1")])]}),"instanceName":"1"});Q2=makeQuery(id+"F39.opBoolean","SPLIT",EDGE,{"disambiguationData":[TD([subQ5])],"derivedFrom":makeQuery(id+"F28.opBoolean","SPLIT",EDGE,{"disambiguationData":[TD([subQ5])],"derivedFrom":makeQuery(id+"F17.opExtrude","CAP_EDGE",EDGE,{"disambiguationData":[OSD([subQ1])],"isStart":true})})});}
            fillet(context, id + "F59", {"entities" : qUnion([Q0, Q1, Q2]), "radius" : 1 * mm, "tangentPropagation" : true, "allowEdgeOverflow" : false});
        }
        {
            var Q0;
            Q0=qCreatedBy(makeId("Top.planeOp"),FACE);
            var sketch = newSketch(context, id + "F60", { "sketchPlane" : qUnion([Q0])});
            skLineSegment(sketch, "E53.bottom", {"start": v(26, -18) * mm, "end": v(8, -18) * mm});
            skLineSegment(sketch, "E53.top", {"start": v(26, 18) * mm, "end": v(-26, 18) * mm});
            skLineSegment(sketch, "E53.left", {"start": v(26, -18) * mm, "end": v(26, 18) * mm});
            skLineSegment(sketch, "E53.right", {"start": v(-26, -18) * mm, "end": v(-26, 18) * mm});
            skPoint(sketch, "E53.middle", {"position": v(0, 0) * mm});
            skLineSegment(sketch, "E54", {"start": v(0, -6) * mm, "end": v(8, -6) * mm});
            skLineSegment(sketch, "E55", {"start": v(8, -6) * mm, "end": v(8, -18) * mm});
            skLineSegment(sketch, "E56", {"start": v(-8, -18) * mm, "end": v(-8, -6) * mm});
            skLineSegment(sketch, "E57", {"start": v(-8, -6) * mm, "end": v(0, -6) * mm});
            skLineSegment(sketch, "E58.trimOffspring", {"start": v(-8, -18) * mm, "end": v(-26, -18) * mm});
            skSolve(sketch);
        }
        {
            var Q0;
            Q0 = qSketchRegion(id + "F60", true);
            extrude(context, id + "F61", {"entities" : qUnion([Q0]), "depth" : 4 * mm});
        }
        {
            var Q0;
            Q0=qCreatedBy(makeId("Front.planeOp"),FACE);
            var sketch = newSketch(context, id + "F62", { "sketchPlane" : qUnion([Q0])});
            skLineSegment(sketch, "E59", {"start": v(28, 2) * mm, "end": v(26, 0) * mm});
            skLineSegment(sketch, "E60", {"start": v(26, 0) * mm, "end": v(26, 4) * mm});
            skLineSegment(sketch, "E61", {"start": v(26, 4) * mm, "end": v(28, 2) * mm});
            skLineSegment(sketch, "E62", {"start": v(-28, 2) * mm, "end": v(-26, 0) * mm});
            skLineSegment(sketch, "E63", {"start": v(-26, 0) * mm, "end": v(-26, 4) * mm});
            skLineSegment(sketch, "E64", {"start": v(-26, 4) * mm, "end": v(-28, 2) * mm});
            skPoint(sketch, "E65.start.orphan", {"position": v(-26, 2) * mm});
            skPoint(sketch, "E66.start.orphan", {"position": v(26, 2) * mm});
            skSolve(sketch);
        }
        {
            var Q0;
            Q0 = qSketchRegion(id + "F62", true);
            extrude(context, id + "F63", {"entities" : qUnion([Q0]), "endBound" : BoundingType.SYMMETRIC, "depth" : 36 * mm});
        }
        {
            var Q0;
            Q0=makeQuery(id+"F61.opExtrude","SWEPT_BODY",BODY,{"disambiguationData":[OSD([sQuery(id+"F60.wireOp",EDGE,"E53.bottom"),sQuery(id+"F60.wireOp",EDGE,"E53.top"),sQuery(id+"F60.wireOp",EDGE,"E53.left"),sQuery(id+"F60.wireOp",EDGE,"E53.right"),sQuery(id+"F60.wireOp",EDGE,"E54"),sQuery(id+"F60.wireOp",EDGE,"E55"),sQuery(id+"F60.wireOp",EDGE,"E56"),sQuery(id+"F60.wireOp",EDGE,"E57"),sQuery(id+"F60.wireOp",EDGE,"E58.trimOffspring")])]});
            transform(context, id + "F64", {"entities" : qUnion([Q0]), "transformType" : TransformType.TRANSLATION_3D, "dx" : 0 * mm, "dy" : 0 * mm, "dz" : -4 * mm, "makeCopy" : false});
        }
    });
